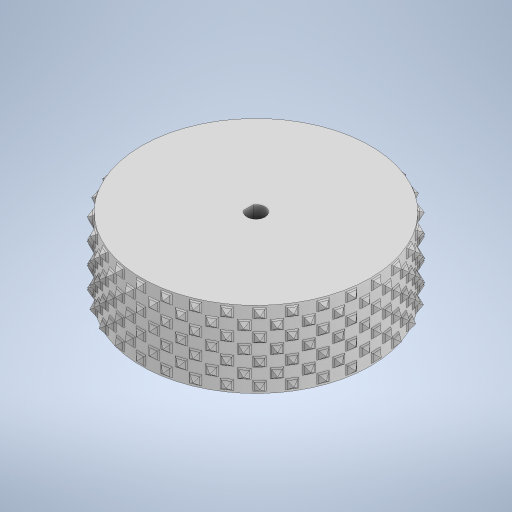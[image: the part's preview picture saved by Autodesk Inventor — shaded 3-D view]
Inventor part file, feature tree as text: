
AUTODESK INVENTOR PART (.ipt)
format: ipt  version: 2024.2 (Build 282272000, 272)  size: 12,252,160 bytes
history: native  units: in
note: dims shown in document units (in); Inventor stores cm internally (conversion verified against a paired STEP export)
features: chamfer x11, extrude x2, pattern_circular x2, sketch x2, plane x1, fillet x1
ambient origin geometry x8: Origin, YZ Plane, XZ Plane, XY Plane, X Axis, Y Axis, Z Axis, Center Point
bodies: Solid1 (feature_tree)
feature tree (19):
  extrude  "Extrusion1"  Depth=0.2362in
  plane  "Work Plane1"
  extrude  "Extrusion2"  Depth=0.125in TaperAngle=0.0deg
  chamfer  "Chamfer18"  Distance=0.125in
  fillet  "Fillet1"  Radius=0.125in
  pattern_circular  "Circular Pattern3"  [2 undecoded]
  chamfer  "Chamfer8"  Distance=0.125in
  chamfer  "Chamfer9"  Distance=0.15in
  chamfer  "Chamfer10"  Distance=0.125in
  chamfer  "Chamfer11"  Distance=0.125in
  chamfer  "Chamfer12"  Distance=0.15in
  chamfer  "Chamfer13"  Distance=0.125in
  chamfer  "Chamfer14"  Distance=0.125in
  chamfer  "Chamfer15"  Distance=0.15in
  chamfer  "Chamfer16"  Distance=0.5in
  chamfer  "Chamfer17"  Distance=0.1in Angle=45.0deg
  pattern_circular  "Circular Pattern2"  Angle=45.0deg  [1 undecoded]
  sketch  "Sketch1"  dims[d0=3.0in d1=0.2362in]
  sketch  "Sketch2"  dims[d2=0.2165in d3=1.0in d4=0.0in d5=0.125in d6=0.125in d7=0.125in d8=0.125in d9=0.15in d10=0.125in d11=0.125in d12=0.15in d16=0.125in d17=0.125in d19=0.15in d20=0.125in d21=0.125in d22=0.125in d23=0.125in d24=0.15in d25=0.125in d26=0.125in d27=0.15in d33=0.065in d34=0.0in d62=0.5in d63=0.1in d64=0.075in d65=45.0deg d66=0.1in d67=0.075in d68=45.0deg d69=0.1in d70=0.075in d71=45.0deg d72=0.1in d73=0.075in d74=45.0deg d75=0.1in d76=0.075in d77=45.0deg d78=0.1in d79=0.075in d80=45.0deg d81=0.1in d82=0.075in d83=45.0deg d84=0.1in d85=0.075in d86=45.0deg d87=0.1in d88=0.075in d89=45.0deg d90=0.1in d91=0.075in d92=45.0deg d93=9.4488in d94=360.0deg d96=0.0625in d97=0.0813in d99=0.1375in d100=0.0813in d101=0.0125in d102=0.0625in d103=0.125in d104=45.0deg d105=12.2047in d106=360.0deg d108=0.125in d107=0.0in]
note: 3 required parameter values undecoded (feature->parameter linkage not recoverable at this tier; creation-order binding heuristic only, values carry confidence <= 0.55)
